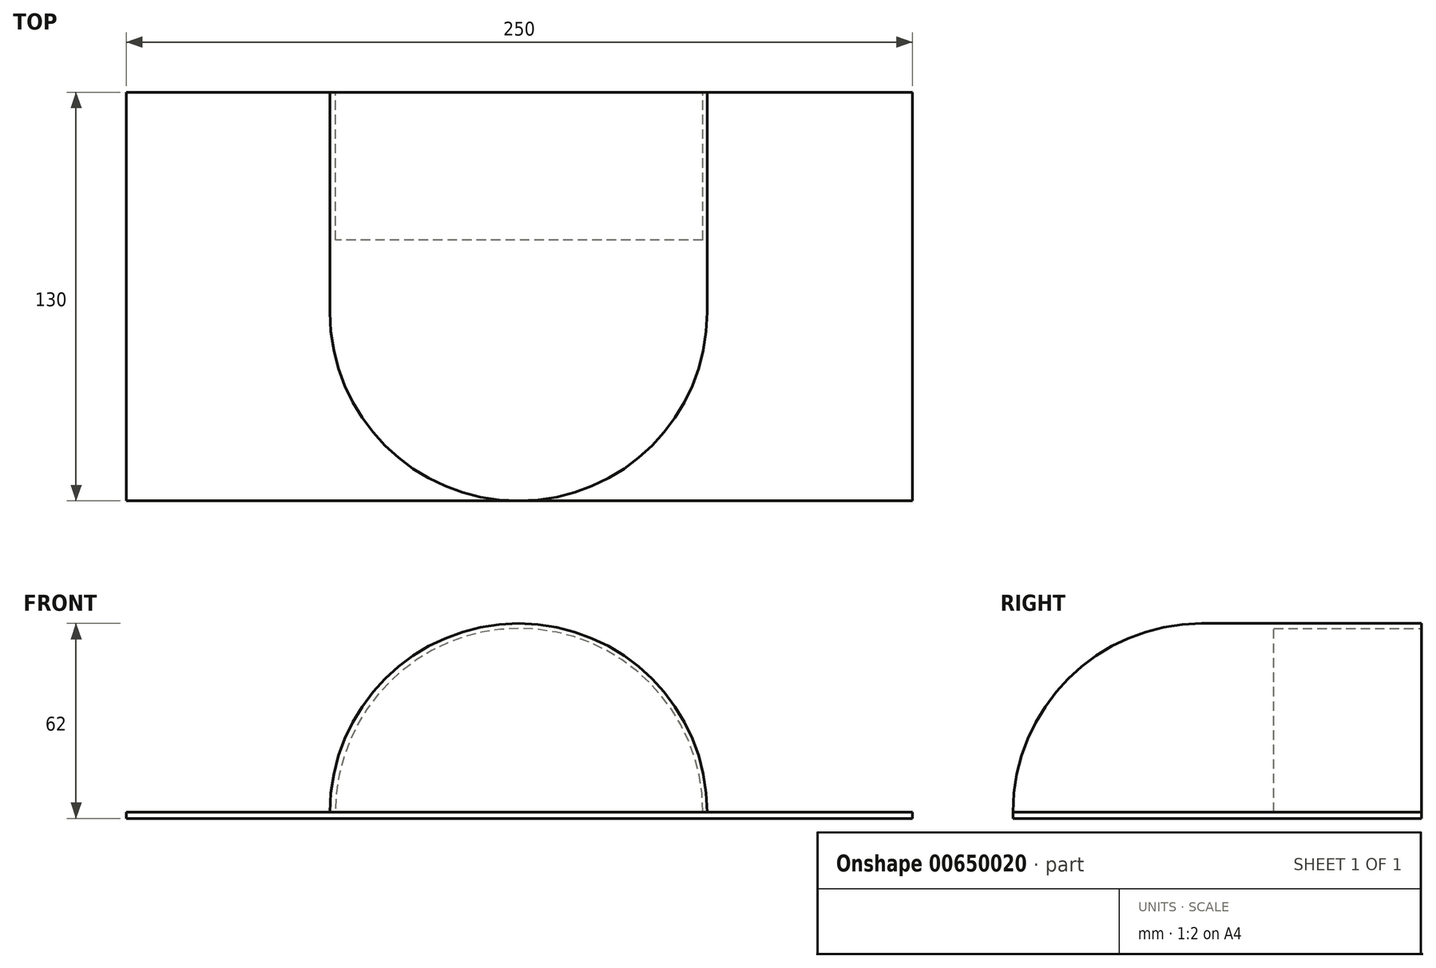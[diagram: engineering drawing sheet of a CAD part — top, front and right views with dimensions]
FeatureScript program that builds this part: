
annotation { "Feature Type Name" : "Feature", "Feature Type Description" : "" }
export const myFeature = defineFeature(function(context is Context, id is Id, definition is map)
    precondition{}
    {
        {
            var Q0;
            Q0=qCreatedBy(makeId("Top.planeOp"),FACE);
            var sketch = newSketch(context, id + "F0", { "sketchPlane" : qUnion([Q0])});
            skLineSegment(sketch, "E0.bottom", {"start": v(0, 0) * mm, "end": v(-250, 0) * mm});
            skLineSegment(sketch, "E0.top", {"start": v(0, -130) * mm, "end": v(-250, -130) * mm});
            skLineSegment(sketch, "E0.left", {"start": v(0, 0) * mm, "end": v(0, -130) * mm});
            skLineSegment(sketch, "E0.right", {"start": v(-250, 0) * mm, "end": v(-250, -130) * mm});
            skSolve(sketch);
        }
        {
            var Q0;
            Q0=qCreatedBy(makeId("Front.planeOp"),FACE);
            var sketch = newSketch(context, id + "F1", { "sketchPlane" : qUnion([Q0])});
            skLineSegment(sketch, "E1", {"start": v(0, 0) * mm, "end": v(-250.54, 0) * mm});
            skArc(sketch, "E2", {"start": v(-65.27, 0) * mm, "mid": v(-125.27, 60) * mm, "end": v(-185.27, 0) * mm});
            skLineSegment(sketch, "E3", {"start": v(4173.46, -3608.09) * mm, "end": v(4422.6, -3608.09) * mm});
            skArc(sketch, "E4", {"start": v(-67.5, 0) * mm, "mid": v(-125.27, 57.77) * mm, "end": v(-183.04, 0) * mm});
            skSolve(sketch);
        }
        {
            var Q0;
            Q0=makeQuery(id+"F0.imprint","IMPRINT",FACE,{"disambiguationData":[TD([[makeQuery(id+"F0.imprint","IMPRINT",EDGE,{"derivedFrom":sQuery(id+"F0.wireOp",EDGE,"E0.bottom")}),1.0]])]});
            extrude(context, id + "F2", {"entities" : qUnion([Q0]), "oppositeDirection" : true, "depth" : 2 * mm, "offsetDistance" : 25 * mm});
        }
        {
            var Q0;
            {var subQ0=sQuery(id+"F1.wireOp",EDGE,"E2");Q0=makeQuery(id+"F1.imprint","IMPRINT",FACE,{"disambiguationData":[TD([[makeQuery(id+"F1.imprint","IMPRINT",EDGE,{"derivedFrom":subQ0}),1.0]])]});}
            var Q1;
            {var subQ0=sQuery(id+"F1.wireOp",EDGE,"E4");Q1=makeQuery(id+"F1.imprint","IMPRINT",FACE,{"disambiguationData":[TD([[makeQuery(id+"F1.imprint","IMPRINT",EDGE,{"derivedFrom":subQ0}),1.0]])]});}
            extrude(context, id + "F3", {"entities" : qUnion([Q0, Q1]), "operationType" : NewBodyOperationType.ADD, "depth" : 130 * mm, "offsetDistance" : 25 * mm});
        }
        {
            var Q0;
            Q0=makeQuery(id+"F3.opExtrude","CAP_EDGE",EDGE,{"disambiguationData":[OSD([sQuery(id+"F1.wireOp",EDGE,"E2")])],"isStart":false});
            fillet(context, id + "F4", {"entities" : qUnion([Q0]), "radius" : 60 * mm, "tangentPropagation" : true, "allowEdgeOverflow" : false});
        }
        {
            var Q0;
            Q0=qCreatedBy(makeId("Front.planeOp"),FACE);
            var sketch = newSketch(context, id + "F5", { "sketchPlane" : qUnion([Q0])});
            skLineSegment(sketch, "E5", {"start": v(0, 0) * mm, "end": v(-250.16, 0) * mm});
            skArc(sketch, "E6", {"start": v(-66.64, 0) * mm, "mid": v(-125.08, 58.44) * mm, "end": v(-183.52, 0) * mm});
            skSolve(sketch);
        }
        {
            var Q0;
            {var subQ0=sQuery(id+"F5.wireOp",EDGE,"E6");Q0=makeQuery(id+"F5.imprint","IMPRINT",FACE,{"disambiguationData":[TD([[makeQuery(id+"F5.imprint","IMPRINT",EDGE,{"derivedFrom":subQ0}),1.0]])]});}
            extrude(context, id + "F6", {"entities" : qUnion([Q0]), "operationType" : NewBodyOperationType.REMOVE, "depth" : 47 * mm, "offsetDistance" : 25 * mm});
        }
    });
